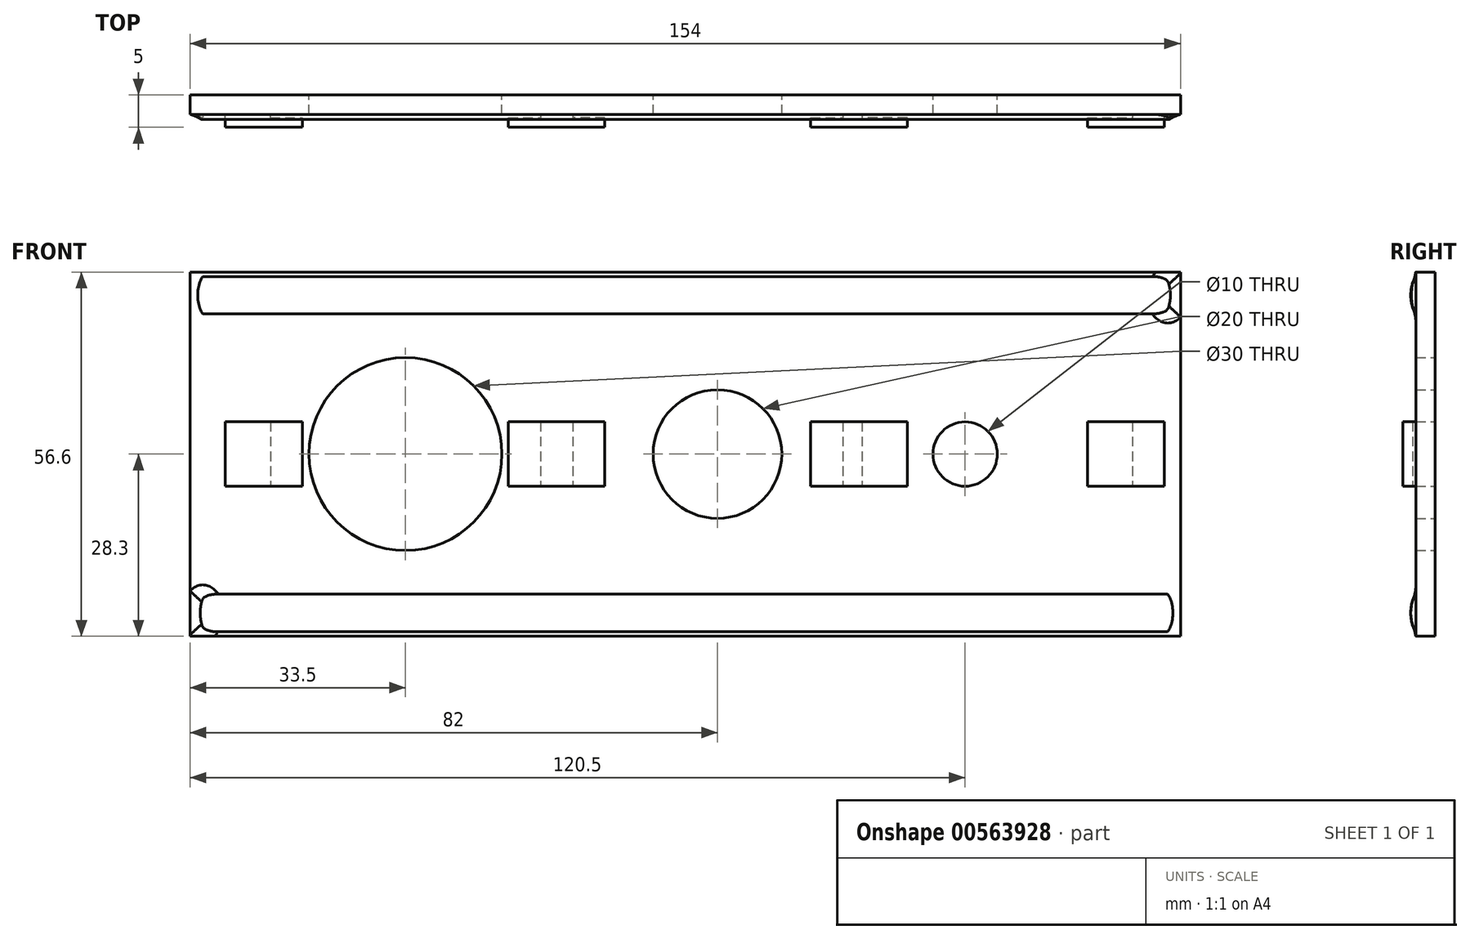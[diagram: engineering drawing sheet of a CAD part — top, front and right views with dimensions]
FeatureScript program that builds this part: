
annotation { "Feature Type Name" : "Feature", "Feature Type Description" : "" }
export const myFeature = defineFeature(function(context is Context, id is Id, definition is map)
    precondition{}
    {
        {
            var Q0;
            Q0=qCreatedBy(makeId("Front.planeOp"),FACE);
            var sketch = newSketch(context, id + "F0", { "sketchPlane" : qUnion([Q0])});
            skLineSegment(sketch, "E0.bottom", {"start": v(77, 28.3) * mm, "end": v(-77, 28.3) * mm});
            skLineSegment(sketch, "E0.top", {"start": v(77, -28.3) * mm, "end": v(-77, -28.3) * mm});
            skLineSegment(sketch, "E0.left", {"start": v(77, 28.3) * mm, "end": v(77, -28.3) * mm});
            skLineSegment(sketch, "E0.right", {"start": v(-77, 28.3) * mm, "end": v(-77, -28.3) * mm});
            skPoint(sketch, "E0.middle", {"position": v(0, 0) * mm});
            skSolve(sketch);
        }
        {
            var Q0;
            Q0 = qSketchRegion(id + "F0", true);
            extrude(context, id + "F1", {"entities" : qUnion([Q0]), "depth" : 3 * mm, "offsetDistance" : 25 * mm});
        }
        {
            var Q0;
            Q0=qCreatedBy(makeId("Front.planeOp"),FACE);
            var sketch = newSketch(context, id + "F2", { "sketchPlane" : qUnion([Q0])});
            skCircle(sketch, "E1", {"center": v(-43.5, 0) * mm, "radius": 15 * mm});
            skCircle(sketch, "E2", {"center": v(5, 0) * mm, "radius": 10 * mm});
            skCircle(sketch, "E3", {"center": v(43.5, 0) * mm, "radius": 5 * mm});
            skSolve(sketch);
        }
        {
            var Q0;
            Q0 = qSketchRegion(id + "F2", true);
            extrude(context, id + "F3", {"entities" : qUnion([Q0]), "operationType" : NewBodyOperationType.REMOVE, "depth" : 3 * mm, "offsetDistance" : 25 * mm});
        }
        {
            var Q0;
            Q0=qCreatedBy(makeId("Right.planeOp"),FACE);
            var sketch = newSketch(context, id + "F4", { "sketchPlane" : qUnion([Q0])});
            skEllipse(sketch, "E4", {"center": v(-1.9, 24.7) * mm, "majorRadius": 3.56 * mm, "minorRadius": 1.9 * mm, "majorAxis": v(0, -1)});
            skEllipse(sketch, "E5", {"center": v(-1.9, -24.7) * mm, "majorRadius": 3.6 * mm, "minorRadius": 1.9 * mm, "majorAxis": v(0, -1)});
            skSolve(sketch);
        }
        {
            var Q0;
            Q0 = qSketchRegion(id + "F4", true);
            extrude(context, id + "F5", {"entities" : qUnion([Q0]), "operationType" : NewBodyOperationType.ADD, "endBound" : BoundingType.SYMMETRIC, "depth" : 150 * mm, "offsetDistance" : 25 * mm});
        }
        {
            var Q0;
            Q0=makeQuery(id+"F5.opExtrude","CAP_FACE",FACE,{"disambiguationData":[OSD([sQuery(id+"F4.wireOp",EDGE,"E4")])],"isStart":true});
            var sketch = newSketch(context, id + "F6", { "sketchPlane" : qUnion([Q0])});
            skSolve(sketch);
        }
        {
            var Q0;
            Q0=makeQuery(id+"F5.opExtrude","CAP_FACE",FACE,{"disambiguationData":[OSD([sQuery(id+"F4.wireOp",EDGE,"E5")])],"isStart":true});
            var sketch = newSketch(context, id + "F7", { "sketchPlane" : qUnion([Q0])});
            skSolve(sketch);
        }
        {
            var Q0;
            {var subQ0=sQuery(id+"F4.wireOp",EDGE,"E5");Q0=makeQuery(id+"F7.imprint","IMPRINT",FACE,{"disambiguationData":[TD([[makeQuery(id+"F7.imprint","IMPRINT",EDGE,{"derivedFrom":makeQuery(id+"F5.opExtrude","CAP_EDGE",EDGE,{"disambiguationData":[OSD([subQ0])],"isStart":true})}),-1.0]])]});}
            var Q1;
            Q1=makeQuery(id+"F5.boolean.opBoolean","INTERSECT",EDGE,{"derivedFrom":[makeQuery(id+"F1.opExtrude","CAP_FACE",FACE,{"disambiguationData":[OSD([sQuery(id+"F0.wireOp",EDGE,"E0.bottom"),sQuery(id+"F0.wireOp",EDGE,"E0.top"),sQuery(id+"F0.wireOp",EDGE,"E0.left"),sQuery(id+"F0.wireOp",EDGE,"E0.right")])],"isStart":false}),makeQuery(id+"F5.opExtrude","CAP_FACE",FACE,{"disambiguationData":[OSD([sQuery(id+"F4.wireOp",EDGE,"E5")])],"isStart":true})]});
            revolve(context, id + "F8", {"operationType" : NewBodyOperationType.ADD, "entities" : qUnion([Q0]), "axis" : qUnion([Q1]), "revolveType" : RevolveType.FULL});
        }
        {
            var Q0;
            {var subQ0=sQuery(id+"F4.wireOp",EDGE,"E4");Q0=makeQuery(id+"F6.imprint","IMPRINT",FACE,{"disambiguationData":[TD([[makeQuery(id+"F6.imprint","IMPRINT",EDGE,{"derivedFrom":makeQuery(id+"F5.opExtrude","CAP_EDGE",EDGE,{"disambiguationData":[OSD([subQ0])],"isStart":true})}),-1.0]])]});}
            var Q1;
            Q1=makeQuery(id+"F5.boolean.opBoolean","INTERSECT",EDGE,{"derivedFrom":[makeQuery(id+"F1.opExtrude","CAP_FACE",FACE,{"disambiguationData":[OSD([sQuery(id+"F0.wireOp",EDGE,"E0.bottom"),sQuery(id+"F0.wireOp",EDGE,"E0.top"),sQuery(id+"F0.wireOp",EDGE,"E0.left"),sQuery(id+"F0.wireOp",EDGE,"E0.right")])],"isStart":false}),makeQuery(id+"F5.opExtrude","CAP_FACE",FACE,{"disambiguationData":[OSD([sQuery(id+"F4.wireOp",EDGE,"E4")])],"isStart":true})]});
            revolve(context, id + "F9", {"operationType" : NewBodyOperationType.ADD, "entities" : qUnion([Q0]), "axis" : qUnion([Q1]), "revolveType" : RevolveType.FULL});
        }
        {
            var Q0;
            Q0=makeQuery(id+"F5.opExtrude","CAP_FACE",FACE,{"disambiguationData":[OSD([sQuery(id+"F4.wireOp",EDGE,"E5")])],"isStart":false});
            var sketch = newSketch(context, id + "F10", { "sketchPlane" : qUnion([Q0])});
            skSolve(sketch);
        }
        {
            var Q0;
            {var subQ0=sQuery(id+"F4.wireOp",EDGE,"E5");Q0=makeQuery(id+"F10.imprint","IMPRINT",FACE,{"disambiguationData":[TD([[makeQuery(id+"F10.imprint","IMPRINT",EDGE,{"derivedFrom":makeQuery(id+"F5.opExtrude","CAP_EDGE",EDGE,{"disambiguationData":[OSD([subQ0])],"isStart":false})}),1.0]])]});}
            var Q1;
            Q1=makeQuery(id+"F5.boolean.opBoolean","INTERSECT",EDGE,{"derivedFrom":[makeQuery(id+"F1.opExtrude","CAP_FACE",FACE,{"disambiguationData":[OSD([sQuery(id+"F0.wireOp",EDGE,"E0.bottom"),sQuery(id+"F0.wireOp",EDGE,"E0.top"),sQuery(id+"F0.wireOp",EDGE,"E0.left"),sQuery(id+"F0.wireOp",EDGE,"E0.right")])],"isStart":false}),makeQuery(id+"F5.opExtrude","CAP_FACE",FACE,{"disambiguationData":[OSD([sQuery(id+"F4.wireOp",EDGE,"E5")])],"isStart":false})]});
            revolve(context, id + "F11", {"operationType" : NewBodyOperationType.ADD, "entities" : qUnion([Q0]), "axis" : qUnion([Q1]), "revolveType" : RevolveType.FULL});
        }
        {
            var Q0;
            Q0=makeQuery(id+"F5.opExtrude","CAP_FACE",FACE,{"disambiguationData":[OSD([sQuery(id+"F4.wireOp",EDGE,"E4")])],"isStart":false});
            var sketch = newSketch(context, id + "F12", { "sketchPlane" : qUnion([Q0])});
            skSolve(sketch);
        }
        {
            var Q0;
            {var subQ0=sQuery(id+"F4.wireOp",EDGE,"E4");Q0=makeQuery(id+"F12.imprint","IMPRINT",FACE,{"disambiguationData":[TD([[makeQuery(id+"F12.imprint","IMPRINT",EDGE,{"derivedFrom":makeQuery(id+"F5.opExtrude","CAP_EDGE",EDGE,{"disambiguationData":[OSD([subQ0])],"isStart":false})}),1.0]])]});}
            var Q1;
            Q1=makeQuery(id+"F5.boolean.opBoolean","INTERSECT",EDGE,{"derivedFrom":[makeQuery(id+"F1.opExtrude","CAP_FACE",FACE,{"disambiguationData":[OSD([sQuery(id+"F0.wireOp",EDGE,"E0.bottom"),sQuery(id+"F0.wireOp",EDGE,"E0.top"),sQuery(id+"F0.wireOp",EDGE,"E0.left"),sQuery(id+"F0.wireOp",EDGE,"E0.right")])],"isStart":false}),makeQuery(id+"F5.opExtrude","CAP_FACE",FACE,{"disambiguationData":[OSD([sQuery(id+"F4.wireOp",EDGE,"E4")])],"isStart":false})]});
            revolve(context, id + "F13", {"operationType" : NewBodyOperationType.ADD, "entities" : qUnion([Q0]), "axis" : qUnion([Q1]), "revolveType" : RevolveType.FULL});
        }
        {
            var Q0;
            Q0=makeQuery(id+"F8.opRevolve","SWEPT_FACE",FACE,{"disambiguationData":[OSD([sQuery(id+"F4.wireOp",EDGE,"E5")])]});
            fillet(context, id + "F14", {"entities" : qUnion([Q0]), "radius" : 6 * mm, "tangentPropagation" : true, "allowEdgeOverflow" : false});
        }
        {
            var Q0;
            Q0=makeQuery(id+"F13.boolean.opBoolean","INTERSECT",EDGE,{"derivedFrom":[makeQuery(id+"F1.opExtrude","CAP_FACE",FACE,{"disambiguationData":[OSD([sQuery(id+"F0.wireOp",EDGE,"E0.bottom"),sQuery(id+"F0.wireOp",EDGE,"E0.top"),sQuery(id+"F0.wireOp",EDGE,"E0.left"),sQuery(id+"F0.wireOp",EDGE,"E0.right")])],"isStart":false}),makeQuery(id+"F13.opRevolve","SWEPT_FACE",FACE,{"disambiguationData":[OSD([sQuery(id+"F4.wireOp",EDGE,"E4")])]})]});
            fillet(context, id + "F15", {"entities" : qUnion([Q0]), "radius" : 6 * mm, "tangentPropagation" : true, "allowEdgeOverflow" : false});
        }
        {
            var Q0;
            Q0=makeQuery(id+"F15.opFillet","SPLIT",FACE,{"disambiguationData":[OD(2.0)],"derivedFrom":makeQuery(id+"F14.opFillet","SPLIT",FACE,{"disambiguationData":[OD(2.0)],"derivedFrom":makeQuery(id+"F1.opExtrude","CAP_FACE",FACE,{"disambiguationData":[OSD([sQuery(id+"F0.wireOp",EDGE,"E0.bottom"),sQuery(id+"F0.wireOp",EDGE,"E0.top"),sQuery(id+"F0.wireOp",EDGE,"E0.left"),sQuery(id+"F0.wireOp",EDGE,"E0.right")])],"isStart":false})})});
            var sketch = newSketch(context, id + "F16", { "sketchPlane" : qUnion([Q0])});
            skLineSegment(sketch, "E6.bottom", {"start": v(-59.5, -5) * mm, "end": v(-71.5, -5) * mm});
            skLineSegment(sketch, "E6.top", {"start": v(-59.5, 5) * mm, "end": v(-71.5, 5) * mm});
            skLineSegment(sketch, "E6.left", {"start": v(-59.5, -5) * mm, "end": v(-59.5, 5) * mm});
            skLineSegment(sketch, "E6.right", {"start": v(-71.5, -5) * mm, "end": v(-71.5, 5) * mm});
            skLineSegment(sketch, "E7.bottom", {"start": v(-27.5, 5) * mm, "end": v(-12.5, 5) * mm});
            skLineSegment(sketch, "E7.top", {"start": v(-27.5, -5) * mm, "end": v(-12.5, -5) * mm});
            skLineSegment(sketch, "E7.left", {"start": v(-27.5, 5) * mm, "end": v(-27.5, -5) * mm});
            skLineSegment(sketch, "E7.right", {"start": v(-12.5, 5) * mm, "end": v(-12.5, -5) * mm});
            skLineSegment(sketch, "E8.bottom", {"start": v(19.5, 5) * mm, "end": v(34.5, 5) * mm});
            skLineSegment(sketch, "E8.top", {"start": v(19.5, -5) * mm, "end": v(34.5, -5) * mm});
            skLineSegment(sketch, "E8.left", {"start": v(19.5, 5) * mm, "end": v(19.5, -5) * mm});
            skLineSegment(sketch, "E8.right", {"start": v(34.5, 5) * mm, "end": v(34.5, -5) * mm});
            skLineSegment(sketch, "E9.bottom", {"start": v(62.5, 5) * mm, "end": v(74.5, 5) * mm});
            skLineSegment(sketch, "E9.top", {"start": v(62.5, -5) * mm, "end": v(74.5, -5) * mm});
            skLineSegment(sketch, "E9.left", {"start": v(62.5, 5) * mm, "end": v(62.5, -5) * mm});
            skLineSegment(sketch, "E9.right", {"start": v(74.5, 5) * mm, "end": v(74.5, -5) * mm});
            skSolve(sketch);
        }
        {
            var Q0;
            Q0 = qSketchRegion(id + "F16", true);
            extrude(context, id + "F17", {"entities" : qUnion([Q0]), "operationType" : NewBodyOperationType.ADD, "depth" : 2 * mm, "offsetDistance" : 25 * mm});
        }
        {
            var Q0;
            Q0=makeQuery(id+"F17.opExtrude","SWEPT_FACE",FACE,{"disambiguationData":[OSD([sQuery(id+"F16.wireOp",EDGE,"E6.bottom")])]});
            var sketch = newSketch(context, id + "F18", { "sketchPlane" : qUnion([Q0])});
            skLineSegment(sketch, "E10.bottom", {"start": v(-64.5, 3.5) * mm, "end": v(-59.5, 3.5) * mm});
            skLineSegment(sketch, "E10.top", {"start": v(-64.5, 3) * mm, "end": v(-59.5, 3) * mm});
            skLineSegment(sketch, "E10.left", {"start": v(-64.5, 3.5) * mm, "end": v(-64.5, 3) * mm});
            skLineSegment(sketch, "E10.right", {"start": v(-59.5, 3.5) * mm, "end": v(-59.5, 3) * mm});
            skSolve(sketch);
        }
        {
            var Q0;
            Q0 = qSketchRegion(id + "F18", true);
            extrude(context, id + "F19", {"entities" : qUnion([Q0]), "operationType" : NewBodyOperationType.REMOVE, "oppositeDirection" : true, "depth" : 10 * mm, "offsetDistance" : 25 * mm});
        }
        {
            var Q0;
            Q0=makeQuery(id+"F17.opExtrude","SWEPT_FACE",FACE,{"disambiguationData":[OSD([sQuery(id+"F16.wireOp",EDGE,"E7.top")])]});
            var sketch = newSketch(context, id + "F20", { "sketchPlane" : qUnion([Q0])});
            skLineSegment(sketch, "E11.bottom", {"start": v(-27.5, 3) * mm, "end": v(-22.5, 3) * mm});
            skLineSegment(sketch, "E11.top", {"start": v(-27.5, 3.5) * mm, "end": v(-22.5, 3.5) * mm});
            skLineSegment(sketch, "E11.left", {"start": v(-27.5, 3) * mm, "end": v(-27.5, 3.5) * mm});
            skLineSegment(sketch, "E11.right", {"start": v(-22.5, 3) * mm, "end": v(-22.5, 3.5) * mm});
            skLineSegment(sketch, "E12.bottom", {"start": v(-12.5, 3) * mm, "end": v(-17.5, 3) * mm});
            skLineSegment(sketch, "E12.top", {"start": v(-12.5, 3.5) * mm, "end": v(-17.5, 3.5) * mm});
            skLineSegment(sketch, "E12.left", {"start": v(-12.5, 3) * mm, "end": v(-12.5, 3.5) * mm});
            skLineSegment(sketch, "E12.right", {"start": v(-17.5, 3) * mm, "end": v(-17.5, 3.5) * mm});
            skSolve(sketch);
        }
        {
            var Q0;
            Q0 = qSketchRegion(id + "F20", true);
            extrude(context, id + "F21", {"entities" : qUnion([Q0]), "operationType" : NewBodyOperationType.REMOVE, "oppositeDirection" : true, "depth" : 10 * mm, "offsetDistance" : 25 * mm});
        }
        {
            var Q0;
            Q0=makeQuery(id+"F17.opExtrude","SWEPT_FACE",FACE,{"disambiguationData":[OSD([sQuery(id+"F16.wireOp",EDGE,"E8.top")])]});
            var sketch = newSketch(context, id + "F22", { "sketchPlane" : qUnion([Q0])});
            skLineSegment(sketch, "E13.bottom", {"start": v(19.5, 3) * mm, "end": v(24.5, 3) * mm});
            skLineSegment(sketch, "E13.top", {"start": v(19.5, 3.5) * mm, "end": v(24.5, 3.5) * mm});
            skLineSegment(sketch, "E13.left", {"start": v(19.5, 3) * mm, "end": v(19.5, 3.5) * mm});
            skLineSegment(sketch, "E13.right", {"start": v(24.5, 3) * mm, "end": v(24.5, 3.5) * mm});
            skLineSegment(sketch, "E14.bottom", {"start": v(34.5, 3) * mm, "end": v(27.5, 3) * mm});
            skLineSegment(sketch, "E14.top", {"start": v(34.5, 3.5) * mm, "end": v(27.5, 3.5) * mm});
            skLineSegment(sketch, "E14.left", {"start": v(34.5, 3) * mm, "end": v(34.5, 3.5) * mm});
            skLineSegment(sketch, "E14.right", {"start": v(27.5, 3) * mm, "end": v(27.5, 3.5) * mm});
            skSolve(sketch);
        }
        {
            var Q0;
            Q0 = qSketchRegion(id + "F22", true);
            extrude(context, id + "F23", {"entities" : qUnion([Q0]), "operationType" : NewBodyOperationType.REMOVE, "oppositeDirection" : true, "depth" : 10 * mm, "offsetDistance" : 25 * mm});
        }
        {
            var Q0;
            Q0=makeQuery(id+"F17.opExtrude","SWEPT_FACE",FACE,{"disambiguationData":[OSD([sQuery(id+"F16.wireOp",EDGE,"E9.top")])]});
            var sketch = newSketch(context, id + "F24", { "sketchPlane" : qUnion([Q0])});
            skLineSegment(sketch, "E15.bottom", {"start": v(62.5, 3) * mm, "end": v(69.5, 3) * mm});
            skLineSegment(sketch, "E15.top", {"start": v(62.5, 3.5) * mm, "end": v(69.5, 3.5) * mm});
            skLineSegment(sketch, "E15.left", {"start": v(62.5, 3) * mm, "end": v(62.5, 3.5) * mm});
            skLineSegment(sketch, "E15.right", {"start": v(69.5, 3) * mm, "end": v(69.5, 3.5) * mm});
            skSolve(sketch);
        }
        {
            var Q0;
            Q0 = qSketchRegion(id + "F24", true);
            extrude(context, id + "F25", {"entities" : qUnion([Q0]), "operationType" : NewBodyOperationType.REMOVE, "oppositeDirection" : true, "depth" : 10 * mm, "offsetDistance" : 25 * mm});
        }
    });
